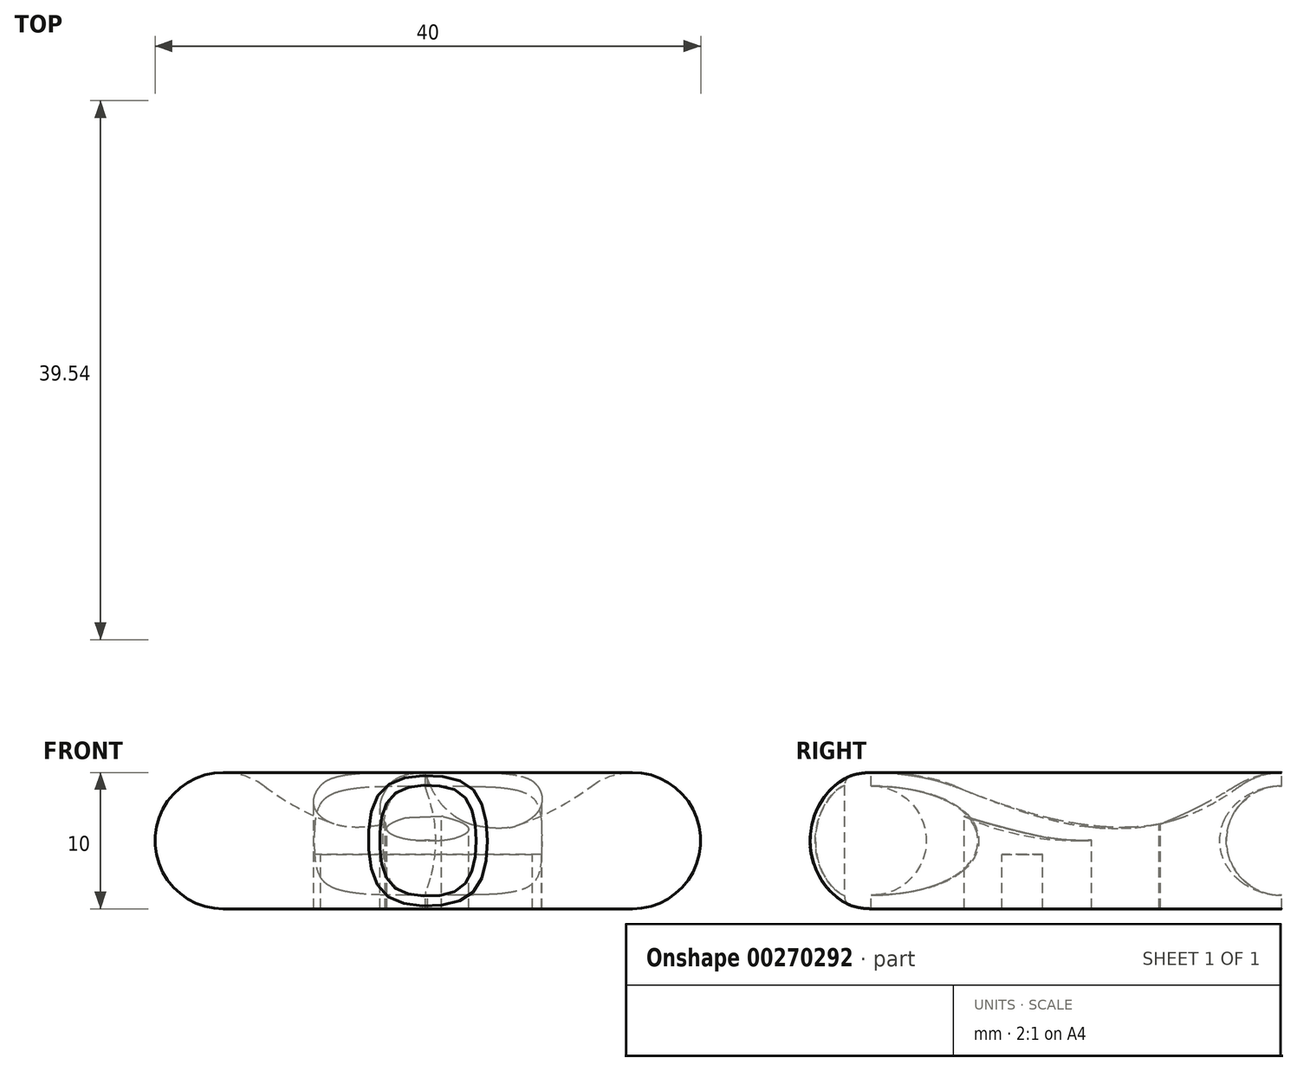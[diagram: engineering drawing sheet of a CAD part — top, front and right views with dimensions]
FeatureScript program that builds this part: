
annotation { "Feature Type Name" : "Feature", "Feature Type Description" : "" }
export const myFeature = defineFeature(function(context is Context, id is Id, definition is map)
    precondition{}
    {
        {
            var Q0;
            Q0=qCreatedBy(makeId("Front.planeOp"),FACE);
            var sketch = newSketch(context, id + "F0", { "sketchPlane" : qUnion([Q0])});
            skArc(sketch, "E0", {"start": v(-12, 9) * mm, "mid": v(-19.74, 6.58) * mm, "end": v(-15, 0) * mm});
            skArc(sketch, "E1", {"start": v(-12, 9) * mm, "mid": v(-6.32, 6.03) * mm, "end": v(0, 5) * mm});
            skLineSegment(sketch, "E2", {"start": v(-15, 0) * mm, "end": v(0, 0) * mm});
            skLineSegment(sketch, "E3", {"start": v(0, 0) * mm, "end": v(0, 5) * mm});
            skSolve(sketch);
        }
        {
            var Q0;
            Q0=makeQuery(id+"F0.imprint","IMPRINT",FACE,{"disambiguationData":[TD([[makeQuery(id+"F0.imprint","IMPRINT",EDGE,{"derivedFrom":sQuery(id+"F0.wireOp",EDGE,"E0")}),1.0]])]});
            var Q1;
            Q1=sQuery(id+"F0.wireOp",EDGE,"E3");
            revolve(context, id + "F1", {"entities" : qUnion([Q0]), "axis" : qUnion([Q1]), "revolveType" : RevolveType.FULL});
        }
        {
            var Q0;
            Q0=qCreatedBy(makeId("Top.planeOp"),FACE);
            cPlane(context, id + "F2", {"entities" : qUnion([Q0]), "cplaneType" : CPlaneType.OFFSET, "offset" : 10 * mm, "width" : 150 * mm, "height" : 150 * mm});
        }
        {
            var Q0;
            Q0=qCreatedBy(id+"F2.planeOp",FACE);
            var sketch = newSketch(context, id + "F3", { "sketchPlane" : qUnion([Q0])});
            skArc(sketch, "E4", {"start": v(-0.27, 14.86) * mm, "mid": v(-0.4, 14.76) * mm, "end": v(-0.54, 14.66) * mm});
            skArc(sketch, "E5", {"start": v(-0.54, 14.66) * mm, "mid": v(-0.66, 14.56) * mm, "end": v(-0.77, 14.45) * mm});
            skArc(sketch, "E6", {"start": v(-0.77, 14.45) * mm, "mid": v(-0.9, 14.34) * mm, "end": v(-1.02, 14.23) * mm});
            skArc(sketch, "E7", {"start": v(-1.02, 14.23) * mm, "mid": v(-1.16, 14.1) * mm, "end": v(-1.3, 13.95) * mm});
            skArc(sketch, "E8", {"start": v(-1.3, 13.95) * mm, "mid": v(-1.72, 13.49) * mm, "end": v(-2.1, 13) * mm});
            skArc(sketch, "E9", {"start": v(-2.1, 13) * mm, "mid": v(-2.45, 12.5) * mm, "end": v(-2.74, 11.98) * mm});
            skArc(sketch, "E10", {"start": v(-2.74, 11.98) * mm, "mid": v(-3, 11.45) * mm, "end": v(-3.2, 10.9) * mm});
            skArc(sketch, "E11", {"start": v(-3.2, 10.9) * mm, "mid": v(-3.35, 10.33) * mm, "end": v(-3.47, 9.76) * mm});
            skArc(sketch, "E12", {"start": v(-3.47, 9.76) * mm, "mid": v(-3.49, 9.6) * mm, "end": v(-3.5, 9.43) * mm});
            skArc(sketch, "E13", {"start": v(-3.5, 9.43) * mm, "mid": v(-3.51, 9.22) * mm, "end": v(-3.52, 9) * mm});
            skArc(sketch, "E14", {"start": v(-3.52, 9) * mm, "mid": v(-3.52, 8.78) * mm, "end": v(-3.52, 8.57) * mm});
            skArc(sketch, "E15", {"start": v(-3.52, 8.57) * mm, "mid": v(-3.52, 8.4) * mm, "end": v(-3.5, 8.22) * mm});
            skArc(sketch, "E16", {"start": v(-3.5, 8.22) * mm, "mid": v(-3.48, 8) * mm, "end": v(-3.45, 7.77) * mm});
            skArc(sketch, "E17", {"start": v(-3.45, 7.77) * mm, "mid": v(-3.42, 7.55) * mm, "end": v(-3.38, 7.33) * mm});
            skArc(sketch, "E18", {"start": v(-3.38, 7.33) * mm, "mid": v(-3.33, 7.1) * mm, "end": v(-3.27, 6.89) * mm});
            skArc(sketch, "E19", {"start": v(-3.27, 6.89) * mm, "mid": v(-3.2, 6.65) * mm, "end": v(-3.14, 6.42) * mm});
            skArc(sketch, "E20", {"start": v(-3.14, 6.42) * mm, "mid": v(-3.1, 6.33) * mm, "end": v(-3.08, 6.24) * mm});
            skArc(sketch, "E21", {"start": v(-3.08, 6.24) * mm, "mid": v(-3.07, 6.2) * mm, "end": v(-3.07, 6.17) * mm});
            skArc(sketch, "E22", {"start": v(-3.07, 6.17) * mm, "mid": v(-3.07, 6.15) * mm, "end": v(-3.07, 6.12) * mm});
            skArc(sketch, "E23", {"start": v(-3.07, 6.12) * mm, "mid": v(-3.08, 6.1) * mm, "end": v(-3.1, 6.1) * mm});
            skArc(sketch, "E24", {"start": v(-3.1, 6.1) * mm, "mid": v(-3.1, 6.08) * mm, "end": v(-3.12, 6.07) * mm});
            skArc(sketch, "E25", {"start": v(-3.12, 6.07) * mm, "mid": v(-3.12, 6.06) * mm, "end": v(-3.12, 6.06) * mm});
            skArc(sketch, "E26", {"start": v(-3.12, 6.06) * mm, "mid": v(-3.12, 6.07) * mm, "end": v(-3.12, 6.07) * mm});
            skArc(sketch, "E27", {"start": v(-3.12, 6.07) * mm, "mid": v(-3.11, 6.08) * mm, "end": v(-3.1, 6.1) * mm});
            skArc(sketch, "E28", {"start": v(-3.1, 6.1) * mm, "mid": v(-3.1, 6.1) * mm, "end": v(-3.09, 6.11) * mm});
            skArc(sketch, "E29", {"start": v(-3.09, 6.11) * mm, "mid": v(-3.08, 6.12) * mm, "end": v(-3.08, 6.13) * mm});
            skArc(sketch, "E30", {"start": v(-3.08, 6.13) * mm, "mid": v(-3.08, 6.14) * mm, "end": v(-3.08, 6.15) * mm});
            skArc(sketch, "E31", {"start": v(-3.08, 6.15) * mm, "mid": v(-3.08, 6.15) * mm, "end": v(-3.08, 6.15) * mm});
            skArc(sketch, "E32", {"start": v(-3.08, 6.15) * mm, "mid": v(-3.08, 6.16) * mm, "end": v(-3.09, 6.15) * mm});
            skArc(sketch, "E33", {"start": v(-3.09, 6.15) * mm, "mid": v(-3.14, 6.09) * mm, "end": v(-3.2, 6.02) * mm});
            skArc(sketch, "E34", {"start": v(-3.2, 6.02) * mm, "mid": v(-3.26, 5.95) * mm, "end": v(-3.32, 5.87) * mm});
            skArc(sketch, "E35", {"start": v(-3.32, 5.87) * mm, "mid": v(-3.4, 5.78) * mm, "end": v(-3.47, 5.7) * mm});
            skArc(sketch, "E36", {"start": v(-3.47, 5.7) * mm, "mid": v(-4.16, 4.8) * mm, "end": v(-4.82, 3.87) * mm});
            skArc(sketch, "E37", {"start": v(-4.82, 3.87) * mm, "mid": v(-5.41, 2.96) * mm, "end": v(-5.96, 2.04) * mm});
            skArc(sketch, "E38", {"start": v(-5.96, 2.04) * mm, "mid": v(-6.45, 1.12) * mm, "end": v(-6.89, 0.19) * mm});
            skArc(sketch, "E39", {"start": v(-6.89, 0.19) * mm, "mid": v(-7.28, -0.75) * mm, "end": v(-7.62, -1.7) * mm});
            skArc(sketch, "E40", {"start": v(-7.62, -1.7) * mm, "mid": v(-7.92, -2.7) * mm, "end": v(-8.15, -3.7) * mm});
            skArc(sketch, "E41", {"start": v(-8.15, -3.7) * mm, "mid": v(-8.3, -4.65) * mm, "end": v(-8.37, -5.61) * mm});
            skArc(sketch, "E42", {"start": v(-8.37, -5.61) * mm, "mid": v(-8.36, -6.51) * mm, "end": v(-8.28, -7.41) * mm});
            skArc(sketch, "E43", {"start": v(-8.28, -7.41) * mm, "mid": v(-8.12, -8.25) * mm, "end": v(-7.88, -9.08) * mm});
            skArc(sketch, "E44", {"start": v(-7.88, -9.08) * mm, "mid": v(-7.74, -9.46) * mm, "end": v(-7.57, -9.84) * mm});
            skArc(sketch, "E45", {"start": v(-7.57, -9.84) * mm, "mid": v(-7.4, -10.2) * mm, "end": v(-7.2, -10.57) * mm});
            skArc(sketch, "E46", {"start": v(-7.2, -10.57) * mm, "mid": v(-6.98, -10.93) * mm, "end": v(-6.74, -11.27) * mm});
            skArc(sketch, "E47", {"start": v(-6.74, -11.27) * mm, "mid": v(-6.5, -11.6) * mm, "end": v(-6.22, -11.94) * mm});
            skArc(sketch, "E48", {"start": v(-6.22, -11.94) * mm, "mid": v(-6.11, -12.06) * mm, "end": v(-6, -12.18) * mm});
            skArc(sketch, "E49", {"start": v(-6, -12.18) * mm, "mid": v(-5.84, -12.35) * mm, "end": v(-5.68, -12.5) * mm});
            skArc(sketch, "E50", {"start": v(-5.68, -12.5) * mm, "mid": v(-5.5, -12.67) * mm, "end": v(-5.34, -12.83) * mm});
            skArc(sketch, "E51", {"start": v(-5.34, -12.83) * mm, "mid": v(-5.2, -12.96) * mm, "end": v(-5.05, -13.1) * mm});
            skArc(sketch, "E52", {"start": v(-5.05, -13.1) * mm, "mid": v(-4.25, -13.71) * mm, "end": v(-3.38, -14.24) * mm});
            skArc(sketch, "E53", {"start": v(-3.38, -14.24) * mm, "mid": v(-2.52, -14.62) * mm, "end": v(-1.61, -14.88) * mm});
            skArc(sketch, "E54", {"start": v(-1.61, -14.88) * mm, "mid": v(-0.69, -15.02) * mm, "end": v(0.25, -15.02) * mm});
            skArc(sketch, "E55", {"start": v(0.25, -15.02) * mm, "mid": v(1.23, -14.9) * mm, "end": v(2.19, -14.66) * mm});
            skArc(sketch, "E56", {"start": v(2.19, -14.66) * mm, "mid": v(2.42, -14.59) * mm, "end": v(2.65, -14.5) * mm});
            skArc(sketch, "E57", {"start": v(2.65, -14.5) * mm, "mid": v(2.9, -14.4) * mm, "end": v(3.14, -14.3) * mm});
            skArc(sketch, "E58", {"start": v(3.14, -14.3) * mm, "mid": v(3.4, -14.2) * mm, "end": v(3.64, -14.08) * mm});
            skArc(sketch, "E59", {"start": v(3.64, -14.08) * mm, "mid": v(3.9, -13.96) * mm, "end": v(4.14, -13.83) * mm});
            skArc(sketch, "E60", {"start": v(4.14, -13.83) * mm, "mid": v(4.33, -13.73) * mm, "end": v(4.52, -13.62) * mm});
            skArc(sketch, "E61", {"start": v(4.52, -13.62) * mm, "mid": v(4.65, -13.54) * mm, "end": v(4.8, -13.46) * mm});
            skArc(sketch, "E62", {"start": v(4.8, -13.46) * mm, "mid": v(4.9, -13.38) * mm, "end": v(5.02, -13.3) * mm});
            skArc(sketch, "E63", {"start": v(5.02, -13.3) * mm, "mid": v(5.13, -13.2) * mm, "end": v(5.25, -13.12) * mm});
            skArc(sketch, "E64", {"start": v(5.25, -13.12) * mm, "mid": v(5.4, -12.98) * mm, "end": v(5.55, -12.84) * mm});
            skArc(sketch, "E65", {"start": v(5.55, -12.84) * mm, "mid": v(5.73, -12.66) * mm, "end": v(5.92, -12.48) * mm});
            skArc(sketch, "E66", {"start": v(5.92, -12.48) * mm, "mid": v(6.1, -12.3) * mm, "end": v(6.27, -12.1) * mm});
            skArc(sketch, "E67", {"start": v(6.27, -12.1) * mm, "mid": v(6.4, -11.96) * mm, "end": v(6.52, -11.8) * mm});
            skArc(sketch, "E68", {"start": v(6.52, -11.8) * mm, "mid": v(7.1, -11) * mm, "end": v(7.57, -10.15) * mm});
            skArc(sketch, "E69", {"start": v(7.57, -10.15) * mm, "mid": v(7.93, -9.26) * mm, "end": v(8.19, -8.34) * mm});
            skArc(sketch, "E70", {"start": v(8.19, -8.34) * mm, "mid": v(8.34, -7.35) * mm, "end": v(8.37, -6.36) * mm});
            skArc(sketch, "E71", {"start": v(8.37, -6.36) * mm, "mid": v(8.3, -5.28) * mm, "end": v(8.13, -4.2) * mm});
            skArc(sketch, "E72", {"start": v(8.13, -4.2) * mm, "mid": v(8.01, -3.66) * mm, "end": v(7.87, -3.13) * mm});
            skArc(sketch, "E73", {"start": v(7.87, -3.13) * mm, "mid": v(7.7, -2.58) * mm, "end": v(7.51, -2.03) * mm});
            skArc(sketch, "E74", {"start": v(7.51, -2.03) * mm, "mid": v(7.29, -1.46) * mm, "end": v(7.05, -0.89) * mm});
            skArc(sketch, "E75", {"start": v(7.05, -0.89) * mm, "mid": v(6.76, -0.27) * mm, "end": v(6.46, 0.35) * mm});
            skArc(sketch, "E76", {"start": v(6.46, 0.35) * mm, "mid": v(6.4, 0.48) * mm, "end": v(6.33, 0.6) * mm});
            skArc(sketch, "E77", {"start": v(6.33, 0.6) * mm, "mid": v(6.26, 0.75) * mm, "end": v(6.2, 0.9) * mm});
            skArc(sketch, "E78", {"start": v(6.2, 0.9) * mm, "mid": v(6.12, 1.04) * mm, "end": v(6.06, 1.18) * mm});
            skArc(sketch, "E79", {"start": v(6.06, 1.18) * mm, "mid": v(6, 1.29) * mm, "end": v(5.96, 1.4) * mm});
            skArc(sketch, "E80", {"start": v(5.96, 1.4) * mm, "mid": v(5.74, 1.86) * mm, "end": v(5.51, 2.31) * mm});
            skArc(sketch, "E81", {"start": v(5.51, 2.31) * mm, "mid": v(5.26, 2.79) * mm, "end": v(4.99, 3.26) * mm});
            skArc(sketch, "E82", {"start": v(4.99, 3.26) * mm, "mid": v(4.68, 3.78) * mm, "end": v(4.36, 4.29) * mm});
            skArc(sketch, "E83", {"start": v(4.36, 4.29) * mm, "mid": v(3.99, 4.86) * mm, "end": v(3.6, 5.43) * mm});
            skArc(sketch, "E84", {"start": v(3.6, 5.43) * mm, "mid": v(3.36, 5.78) * mm, "end": v(3.13, 6.14) * mm});
            skArc(sketch, "E85", {"start": v(3.13, 6.14) * mm, "mid": v(2.92, 6.47) * mm, "end": v(2.71, 6.8) * mm});
            skArc(sketch, "E86", {"start": v(2.71, 6.8) * mm, "mid": v(2.51, 7.12) * mm, "end": v(2.32, 7.44) * mm});
            skArc(sketch, "E87", {"start": v(2.32, 7.44) * mm, "mid": v(2.13, 7.77) * mm, "end": v(1.94, 8.1) * mm});
            skArc(sketch, "E88", {"start": v(1.94, 8.1) * mm, "mid": v(1.38, 9.16) * mm, "end": v(0.86, 10.24) * mm});
            skArc(sketch, "E89", {"start": v(0.86, 10.24) * mm, "mid": v(0.48, 11.15) * mm, "end": v(0.17, 12.1) * mm});
            skArc(sketch, "E90", {"start": v(0.17, 12.1) * mm, "mid": v(-0.03, 12.87) * mm, "end": v(-0.15, 13.65) * mm});
            skArc(sketch, "E91", {"start": v(-0.15, 13.65) * mm, "mid": v(-0.17, 14.25) * mm, "end": v(-0.06, 14.85) * mm});
            skArc(sketch, "E92", {"start": v(-0.06, 14.85) * mm, "mid": v(-0.05, 14.88) * mm, "end": v(-0.04, 14.92) * mm});
            skArc(sketch, "E93", {"start": v(-0.04, 14.92) * mm, "mid": v(-0.04, 14.95) * mm, "end": v(-0.03, 14.98) * mm});
            skArc(sketch, "E94", {"start": v(-0.03, 14.98) * mm, "mid": v(-0.02, 15) * mm, "end": v(-0.02, 15.03) * mm});
            skArc(sketch, "E95", {"start": v(-0.02, 15.03) * mm, "mid": v(-0.02, 15.03) * mm, "end": v(-0.02, 15.04) * mm});
            skArc(sketch, "E96", {"start": v(-0.02, 15.04) * mm, "mid": v(-0.02, 15.04) * mm, "end": v(-0.03, 15.04) * mm});
            skArc(sketch, "E97", {"start": v(-0.03, 15.04) * mm, "mid": v(-0.06, 15.01) * mm, "end": v(-0.1, 14.99) * mm});
            skArc(sketch, "E98", {"start": v(-0.1, 14.99) * mm, "mid": v(-0.14, 14.96) * mm, "end": v(-0.18, 14.93) * mm});
            skArc(sketch, "E99", {"start": v(-0.18, 14.93) * mm, "mid": v(-0.23, 14.9) * mm, "end": v(-0.27, 14.86) * mm});
            skArc(sketch, "E100", {"start": v(0.53, 0.3) * mm, "mid": v(0.7, 0.02) * mm, "end": v(0.89, -0.25) * mm});
            skArc(sketch, "E101", {"start": v(0.89, -0.25) * mm, "mid": v(1.08, -0.55) * mm, "end": v(1.28, -0.86) * mm});
            skArc(sketch, "E102", {"start": v(1.28, -0.86) * mm, "mid": v(1.49, -1.16) * mm, "end": v(1.7, -1.47) * mm});
            skArc(sketch, "E103", {"start": v(1.7, -1.47) * mm, "mid": v(1.9, -1.77) * mm, "end": v(2.1, -2.07) * mm});
            skArc(sketch, "E104", {"start": v(2.1, -2.07) * mm, "mid": v(2.19, -2.21) * mm, "end": v(2.28, -2.36) * mm});
            skArc(sketch, "E105", {"start": v(2.28, -2.36) * mm, "mid": v(2.36, -2.52) * mm, "end": v(2.44, -2.69) * mm});
            skArc(sketch, "E106", {"start": v(2.44, -2.69) * mm, "mid": v(2.52, -2.86) * mm, "end": v(2.6, -3.04) * mm});
            skArc(sketch, "E107", {"start": v(2.6, -3.04) * mm, "mid": v(2.67, -3.22) * mm, "end": v(2.73, -3.4) * mm});
            skArc(sketch, "E108", {"start": v(2.73, -3.4) * mm, "mid": v(2.87, -3.9) * mm, "end": v(2.95, -4.4) * mm});
            skArc(sketch, "E109", {"start": v(2.95, -4.4) * mm, "mid": v(2.99, -4.86) * mm, "end": v(2.96, -5.33) * mm});
            skArc(sketch, "E110", {"start": v(2.96, -5.33) * mm, "mid": v(2.88, -5.77) * mm, "end": v(2.74, -6.2) * mm});
            skArc(sketch, "E111", {"start": v(2.74, -6.2) * mm, "mid": v(2.55, -6.61) * mm, "end": v(2.31, -7) * mm});
            skArc(sketch, "E112", {"start": v(2.31, -7) * mm, "mid": v(2.2, -7.15) * mm, "end": v(2.08, -7.3) * mm});
            skArc(sketch, "E113", {"start": v(2.08, -7.3) * mm, "mid": v(1.93, -7.45) * mm, "end": v(1.78, -7.6) * mm});
            skArc(sketch, "E114", {"start": v(1.78, -7.6) * mm, "mid": v(1.61, -7.75) * mm, "end": v(1.45, -7.9) * mm});
            skArc(sketch, "E115", {"start": v(1.45, -7.9) * mm, "mid": v(1.29, -8.02) * mm, "end": v(1.13, -8.14) * mm});
            skLineSegment(sketch, "E116", {"start": v(1.13, -8.14) * mm, "end": v(0.99, -8.23) * mm});
            skLineSegment(sketch, "E117", {"start": v(0.99, -8.23) * mm, "end": v(0.65, -8.23) * mm});
            skArc(sketch, "E118", {"start": v(0.65, -8.23) * mm, "mid": v(0.4, -8.22) * mm, "end": v(0.16, -8.21) * mm});
            skArc(sketch, "E119", {"start": v(0.16, -8.21) * mm, "mid": v(-0.1, -8.19) * mm, "end": v(-0.36, -8.16) * mm});
            skArc(sketch, "E120", {"start": v(-0.36, -8.16) * mm, "mid": v(-0.6, -8.12) * mm, "end": v(-0.86, -8.08) * mm});
            skArc(sketch, "E121", {"start": v(-0.86, -8.08) * mm, "mid": v(-1.1, -8.03) * mm, "end": v(-1.32, -7.97) * mm});
            skArc(sketch, "E122", {"start": v(-1.32, -7.97) * mm, "mid": v(-1.43, -7.94) * mm, "end": v(-1.53, -7.9) * mm});
            skArc(sketch, "E123", {"start": v(-1.53, -7.9) * mm, "mid": v(-1.57, -7.9) * mm, "end": v(-1.62, -7.87) * mm});
            skArc(sketch, "E124", {"start": v(-1.62, -7.87) * mm, "mid": v(-1.66, -7.85) * mm, "end": v(-1.7, -7.82) * mm});
            skArc(sketch, "E125", {"start": v(-1.7, -7.82) * mm, "mid": v(-1.75, -7.77) * mm, "end": v(-1.8, -7.72) * mm});
            skArc(sketch, "E126", {"start": v(-1.8, -7.72) * mm, "mid": v(-2.02, -7.5) * mm, "end": v(-2.22, -7.25) * mm});
            skArc(sketch, "E127", {"start": v(-2.22, -7.25) * mm, "mid": v(-2.4, -7) * mm, "end": v(-2.56, -6.73) * mm});
            skArc(sketch, "E128", {"start": v(-2.56, -6.73) * mm, "mid": v(-2.7, -6.46) * mm, "end": v(-2.8, -6.19) * mm});
            skArc(sketch, "E129", {"start": v(-2.8, -6.19) * mm, "mid": v(-2.9, -5.9) * mm, "end": v(-2.96, -5.62) * mm});
            skArc(sketch, "E130", {"start": v(-2.96, -5.62) * mm, "mid": v(-3, -5.36) * mm, "end": v(-3.01, -5.08) * mm});
            skArc(sketch, "E131", {"start": v(-3.01, -5.08) * mm, "mid": v(-3, -4.77) * mm, "end": v(-2.97, -4.46) * mm});
            skArc(sketch, "E132", {"start": v(-2.97, -4.46) * mm, "mid": v(-2.92, -4.15) * mm, "end": v(-2.85, -3.84) * mm});
            skArc(sketch, "E133", {"start": v(-2.85, -3.84) * mm, "mid": v(-2.76, -3.55) * mm, "end": v(-2.65, -3.27) * mm});
            skArc(sketch, "E134", {"start": v(-2.65, -3.27) * mm, "mid": v(-2.48, -2.9) * mm, "end": v(-2.3, -2.52) * mm});
            skArc(sketch, "E135", {"start": v(-2.3, -2.52) * mm, "mid": v(-1.98, -1.94) * mm, "end": v(-1.66, -1.37) * mm});
            skArc(sketch, "E136", {"start": v(-1.66, -1.37) * mm, "mid": v(-1.33, -0.8) * mm, "end": v(-1, -0.23) * mm});
            skArc(sketch, "E137", {"start": v(-1, -0.23) * mm, "mid": v(-0.77, 0.13) * mm, "end": v(-0.54, 0.48) * mm});
            skArc(sketch, "E138", {"start": v(-0.54, 0.48) * mm, "mid": v(-0.47, 0.57) * mm, "end": v(-0.4, 0.67) * mm});
            skArc(sketch, "E139", {"start": v(-0.4, 0.67) * mm, "mid": v(-0.3, 0.77) * mm, "end": v(-0.22, 0.88) * mm});
            skArc(sketch, "E140", {"start": v(-0.22, 0.88) * mm, "mid": v(-0.13, 0.99) * mm, "end": v(-0.04, 1.1) * mm});
            skArc(sketch, "E141", {"start": v(-0.04, 1.1) * mm, "mid": v(-0.03, 1.1) * mm, "end": v(-0.01, 1.1) * mm});
            skArc(sketch, "E142", {"start": v(-0.01, 1.1) * mm, "mid": v(0, 1.1) * mm, "end": v(0, 1.1) * mm});
            skArc(sketch, "E143", {"start": v(0, 1.1) * mm, "mid": v(0.08, 0.98) * mm, "end": v(0.15, 0.87) * mm});
            skArc(sketch, "E144", {"start": v(0.15, 0.87) * mm, "mid": v(0.24, 0.73) * mm, "end": v(0.33, 0.6) * mm});
            skArc(sketch, "E145", {"start": v(0.33, 0.6) * mm, "mid": v(0.43, 0.45) * mm, "end": v(0.53, 0.3) * mm});
            skSolve(sketch);
        }
        {
            var Q0;
            Q0=makeQuery(id+"F3.imprint","IMPRINT",FACE,{"disambiguationData":[TD([[makeQuery(id+"F3.imprint","IMPRINT",EDGE,{"derivedFrom":sQuery(id+"F3.wireOp",EDGE,"E4")}),1.0]])]});
            extrude(context, id + "F4", {"entities" : qUnion([Q0]), "operationType" : NewBodyOperationType.REMOVE, "oppositeDirection" : true, "depth" : 25 * mm});
        }
        {
            var Q0;
            Q0=qCreatedBy(makeId("Top.planeOp"),FACE);
            var sketch = newSketch(context, id + "F5", { "sketchPlane" : qUnion([Q0])});
            skLineSegment(sketch, "E146", {"start": v(10, -5.47) * mm, "end": v(-9.85, -5.47) * mm});
            skLineSegment(sketch, "E147", {"start": v(-9.85, -5.47) * mm, "end": v(-9.85, -2.47) * mm});
            skLineSegment(sketch, "E148", {"start": v(-9.85, -2.47) * mm, "end": v(9.94, -2.47) * mm});
            skLineSegment(sketch, "E149", {"start": v(10, -5.47) * mm, "end": v(9.94, -2.47) * mm});
            skSolve(sketch);
        }
        {
            var Q0;
            Q0=makeQuery(id+"F5.imprint","IMPRINT",FACE,{"disambiguationData":[TD([[makeQuery(id+"F5.imprint","IMPRINT",EDGE,{"derivedFrom":sQuery(id+"F5.wireOp",EDGE,"E146")}),-1.0]])]});
            extrude(context, id + "F6", {"entities" : qUnion([Q0]), "depth" : 4 * mm});
        }
        {
            var Q0;
            Q0=qCreatedBy(makeId("Front.planeOp"),FACE);
            var sketch = newSketch(context, id + "F7", { "sketchPlane" : qUnion([Q0])});
            skCircle(sketch, "E150", {"center": v(-15, 5) * mm, "radius": 3.75 * mm});
            skSolve(sketch);
        }
        {
            var Q0;
            Q0 = qSketchRegion(id + "F7", true);
            var Q1;
            Q1=sQuery(id+"F7.wireOp",EDGE,"E150");
            var Q2;
            Q2=sQuery(id+"F0.wireOp",EDGE,"E3");
            revolve(context, id + "F8", {"operationType" : NewBodyOperationType.ADD, "entities" : qUnion([Q0]), "surfaceEntities" : qUnion([Q1]), "axis" : qUnion([Q2]), "revolveType" : RevolveType.FULL});
        }
        {
            var Q0;
            Q0=qCreatedBy(makeId("Front.planeOp"),FACE);
            var sketch = newSketch(context, id + "F9", { "sketchPlane" : qUnion([Q0])});
            skCircle(sketch, "E151", {"center": v(-15, 5) * mm, "radius": 4 * mm});
            skSolve(sketch);
        }
        {
            var Q0;
            Q0 = qSketchRegion(id + "F9", true);
            var Q1;
            Q1=sQuery(id+"F0.wireOp",EDGE,"E3");
            revolve(context, id + "F10", {"operationType" : NewBodyOperationType.ADD, "entities" : qUnion([Q0]), "axis" : qUnion([Q1]), "revolveType" : RevolveType.FULL});
        }
        {
            var Q0;
            Q0=qCreatedBy(makeId("Top.planeOp"),FACE);
            var sketch = newSketch(context, id + "F11", { "sketchPlane" : qUnion([Q0])});
            skCircle(sketch, "E152", {"center": v(0, -21) * mm, "radius": 4 * mm});
            skSolve(sketch);
        }
        {
            var Q0;
            Q0=makeQuery(id+"F11.imprint","IMPRINT",FACE,{"disambiguationData":[TD([[makeQuery(id+"F11.imprint","IMPRINT",EDGE,{"derivedFrom":sQuery(id+"F11.wireOp",EDGE,"E152")}),1.0]])]});
            var Q1;
            Q1=sQuery(id+"F11.wireOp",EDGE,"E152");
            extrude(context, id + "F12", {"entities" : qUnion([Q0]), "operationType" : NewBodyOperationType.REMOVE, "surfaceEntities" : qUnion([Q1]), "depth" : 24.5 * mm});
        }
        {
            var Q0;
            Q0=makeQuery(id+"F12.boolean.opBoolean","COPY",FACE,{"derivedFrom":makeQuery(id+"F12.opExtrude","SWEPT_FACE",FACE,{"disambiguationData":[OSD([sQuery(id+"F11.wireOp",EDGE,"E152")])]})});
            fillet(context, id + "F13", {"entities" : qUnion([Q0]), "radius" : 0.75 * mm, "tangentPropagation" : true, "allowEdgeOverflow" : false});
        }
    });
